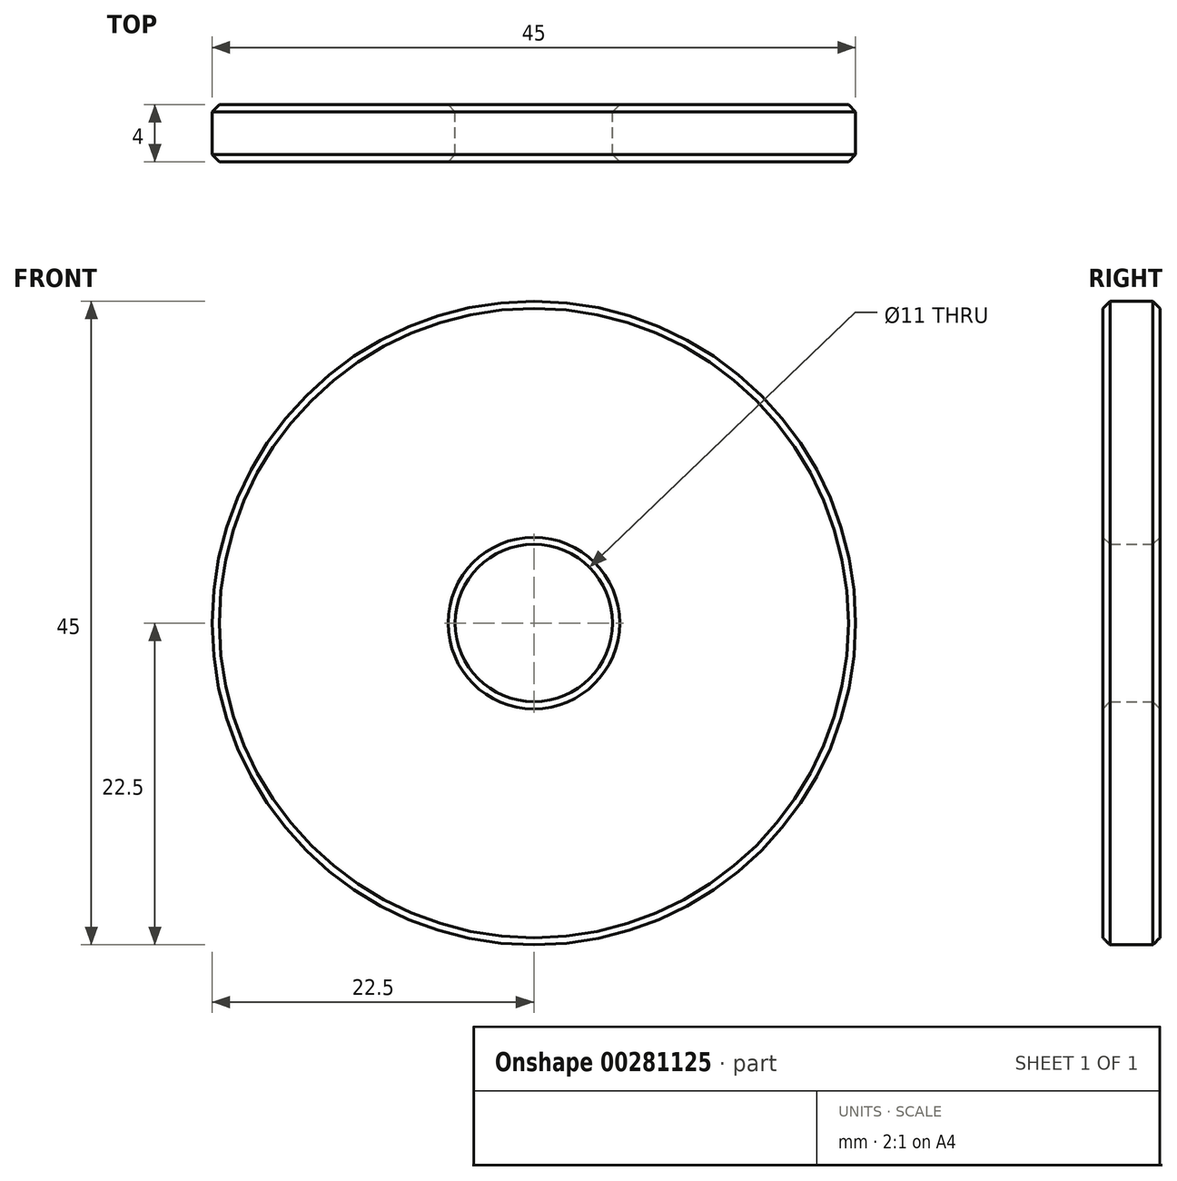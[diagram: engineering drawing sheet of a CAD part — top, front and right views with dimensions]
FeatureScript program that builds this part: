
annotation { "Feature Type Name" : "Feature", "Feature Type Description" : "" }
export const myFeature = defineFeature(function(context is Context, id is Id, definition is map)
    precondition{}
    {
        {
            var Q0;
            Q0=qCreatedBy(makeId("Front.planeOp"),FACE);
            var sketch = newSketch(context, id + "F0", { "sketchPlane" : qUnion([Q0])});
            skCircle(sketch, "E0", {"center": v(0, 0) * mm, "radius": 22.5 * mm});
            skCircle(sketch, "E1", {"center": v(0, 0) * mm, "radius": 5.5 * mm});
            skSolve(sketch);
        }
        {
            var Q0;
            Q0 = qSketchRegion(id + "F0", true);
            extrude(context, id + "F1", {"entities" : qUnion([Q0]), "depth" : 4 * mm});
        }
        {
            var Q0;
            Q0=makeQuery(id+"F1.opExtrude","CAP_EDGE",EDGE,{"disambiguationData":[OSD([sQuery(id+"F0.wireOp",EDGE,"E0")])],"isStart":false});
            var Q1;
            Q1=makeQuery(id+"F1.opExtrude","CAP_EDGE",EDGE,{"disambiguationData":[OSD([sQuery(id+"F0.wireOp",EDGE,"E1")])],"isStart":false});
            var Q2;
            Q2=makeQuery(id+"F1.opExtrude","CAP_EDGE",EDGE,{"disambiguationData":[OSD([sQuery(id+"F0.wireOp",EDGE,"E0")])],"isStart":true});
            var Q3;
            Q3=makeQuery(id+"F1.opExtrude","CAP_EDGE",EDGE,{"disambiguationData":[OSD([sQuery(id+"F0.wireOp",EDGE,"E1")])],"isStart":true});
            chamfer(context, id + "F2", {"entities" : qUnion([Q0, Q1, Q2, Q3]), "width" : .5 * mm, "tangentPropagation" : true});
        }
    });
